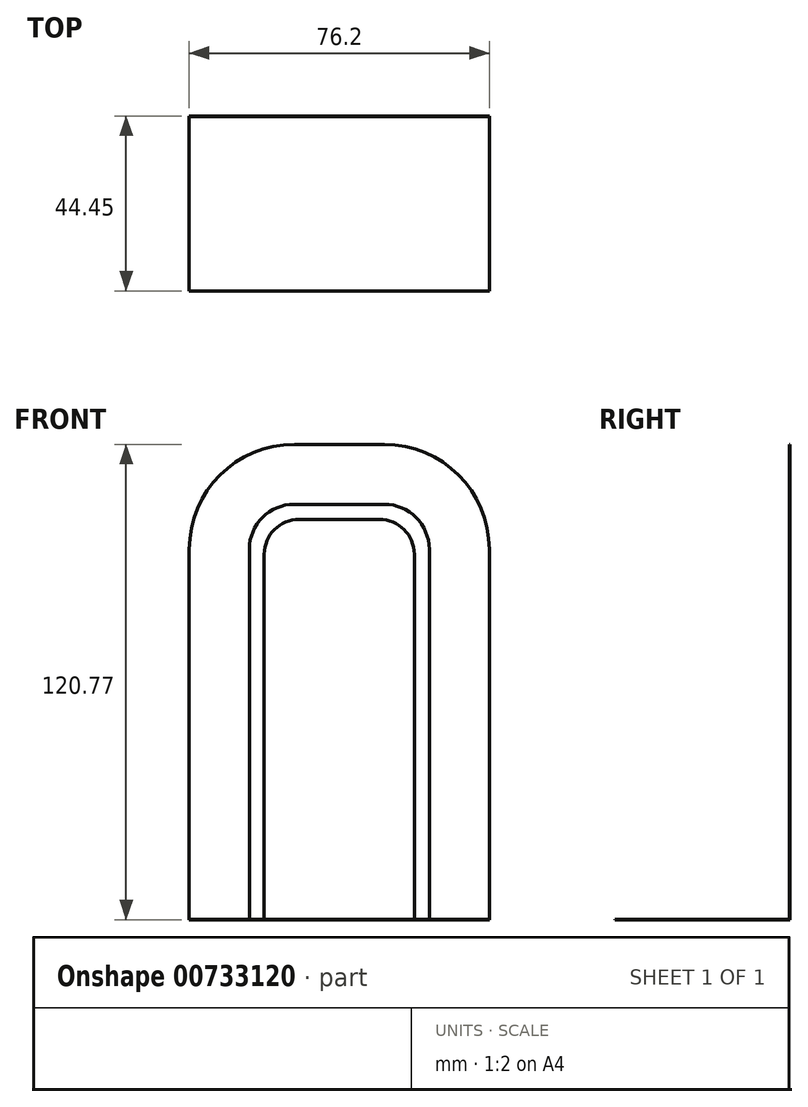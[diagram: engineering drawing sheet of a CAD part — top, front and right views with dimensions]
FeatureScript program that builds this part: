
annotation { "Feature Type Name" : "Feature", "Feature Type Description" : "" }
export const myFeature = defineFeature(function(context is Context, id is Id, definition is map)
    precondition{}
    {
        {
            assignVariable(context, id + "F0", {"name" : "t", "anyValue" : .125});
        }
        {
            var Q0;
            Q0=qCreatedBy(makeId("Front.planeOp"),FACE);
            var sketch = newSketch(context, id + "F1", { "sketchPlane" : qUnion([Q0])});
            skLineSegment(sketch, "E0.bottom", {"start": v(26.67, 120.65) * mm, "end": v(49.53, 120.65) * mm});
            skLineSegment(sketch, "E0.top", {"start": v(0, 0) * mm, "end": v(15.24, 0) * mm});
            skLineSegment(sketch, "E0.left", {"start": v(0, 93.98) * mm, "end": v(0, 0) * mm});
            skLineSegment(sketch, "E0.right", {"start": v(76.2, 93.98) * mm, "end": v(76.2, 0) * mm});
            skPoint(sketch, "E1.visualSharp", {"position": v(0, 120.65) * mm});
            skArc(sketch, "E1.filletArc", {"start": v(26.67, 120.65) * mm, "mid": v(7.81, 112.84) * mm, "end": v(0, 93.98) * mm});
            skPoint(sketch, "E2.visualSharp", {"position": v(76.2, 120.65) * mm});
            skArc(sketch, "E2.filletArc", {"start": v(76.2, 93.98) * mm, "mid": v(68.39, 112.84) * mm, "end": v(49.53, 120.65) * mm});
            skLineSegment(sketch, "E3.0", {"start": v(60.96, 93.98) * mm, "end": v(60.96, 0) * mm});
            skLineSegment(sketch, "E3.1", {"start": v(15.24, 93.98) * mm, "end": v(15.24, 0) * mm});
            skArc(sketch, "E3.2", {"start": v(26.67, 105.41) * mm, "mid": v(18.59, 102.06) * mm, "end": v(15.24, 93.98) * mm});
            skLineSegment(sketch, "E3.3", {"start": v(26.67, 105.41) * mm, "end": v(49.53, 105.41) * mm});
            skArc(sketch, "E3.4", {"start": v(60.96, 93.98) * mm, "mid": v(57.61, 102.06) * mm, "end": v(49.53, 105.41) * mm});
            skLineSegment(sketch, "E4.trimOffspring", {"start": v(60.96, 0) * mm, "end": v(76.2, 0) * mm});
            skSolve(sketch);
        }
        {
            var Q0;
            Q0=qSketchRegion(id+"F1",true);
            extrude(context, id + "F2", {"entities" : qUnion([Q0]), "depth" : (getVariable(context, 't')) * mm, "offsetDistance" : 25.4 * mm});
        }
        {
            var Q0;
            Q0=qCreatedBy(makeId("Top.planeOp"),FACE);
            var sketch = newSketch(context, id + "F3", { "sketchPlane" : qUnion([Q0])});
            skLineSegment(sketch, "E5.bottom", {"start": v(0, 0) * mm, "end": v(76.2, 0) * mm});
            skLineSegment(sketch, "E5.top", {"start": v(0, -44.45) * mm, "end": v(76.2, -44.45) * mm});
            skLineSegment(sketch, "E5.left", {"start": v(0, 0) * mm, "end": v(0, -44.45) * mm});
            skLineSegment(sketch, "E5.right", {"start": v(76.2, 0) * mm, "end": v(76.2, -44.45) * mm});
            skPoint(sketch, "E6", {"position": v(38.1, 0) * mm});
            skSolve(sketch);
        }
        {
            var Q0;
            Q0=qSketchRegion(id+"F3",true);
            extrude(context, id + "F4", {"entities" : qUnion([Q0]), "operationType" : NewBodyOperationType.ADD, "oppositeDirection" : true, "depth" : (getVariable(context, 't')) * mm, "offsetDistance" : 25.4 * mm});
        }
        {
            var Q0;
            Q0=qCreatedBy(makeId("Front.planeOp"),FACE);
            var sketch = newSketch(context, id + "F5", { "sketchPlane" : qUnion([Q0])});
            skLineSegment(sketch, "E7.bottom", {"start": v(27.94, 101.6) * mm, "end": v(48.26, 101.6) * mm});
            skLineSegment(sketch, "E7.top", {"start": v(19.05, 0) * mm, "end": v(57.15, 0) * mm});
            skLineSegment(sketch, "E7.left", {"start": v(19.05, 92.71) * mm, "end": v(19.05, 0) * mm});
            skLineSegment(sketch, "E7.right", {"start": v(57.15, 92.71) * mm, "end": v(57.15, 0) * mm});
            skPoint(sketch, "E8.visualSharp", {"position": v(19.05, 101.6) * mm});
            skArc(sketch, "E8.filletArc", {"start": v(27.94, 101.6) * mm, "mid": v(21.65, 99) * mm, "end": v(19.05, 92.71) * mm});
            skPoint(sketch, "E9.visualSharp", {"position": v(57.15, 101.6) * mm});
            skArc(sketch, "E9.filletArc", {"start": v(57.15, 92.71) * mm, "mid": v(54.55, 99) * mm, "end": v(48.26, 101.6) * mm});
            skPoint(sketch, "E10", {"position": v(38.1, 0) * mm});
            skLineSegment(sketch, "E11.0.1", {"start": v(76.2, 0) * mm, "end": v(60.96, 0) * mm});
            skLineSegment(sketch, "E11.0.3", {"start": v(60.96, 0) * mm, "end": v(15.24, 0) * mm});
            skLineSegment(sketch, "E11.0.5", {"start": v(15.24, 0) * mm, "end": v(0, 0) * mm});
            skLineSegment(sketch, "E11.0.7", {"start": v(0, 0) * mm, "end": v(0, 0) * mm});
            skLineSegment(sketch, "E11.0.9", {"start": v(0, 0) * mm, "end": v(76.2, 0) * mm});
            skLineSegment(sketch, "E11.0.11", {"start": v(67.3, 0) * mm, "end": v(58.42, 0) * mm});
            skSolve(sketch);
        }
        {
            var Q0;
            Q0=makeQuery(id+"F5.imprint","IMPRINT",FACE,{"disambiguationData":[TD([[makeQuery(id+"F5.imprint","IMPRINT",EDGE,{"derivedFrom":sQuery(id+"F5.wireOp",EDGE,"E7.bottom")}),-1.0]])]});
            extrude(context, id + "F6", {"entities" : qUnion([Q0]), "operationType" : NewBodyOperationType.ADD, "depth" : (getVariable(context, 't')) * mm, "offsetDistance" : 25.4 * mm});
        }
    });
